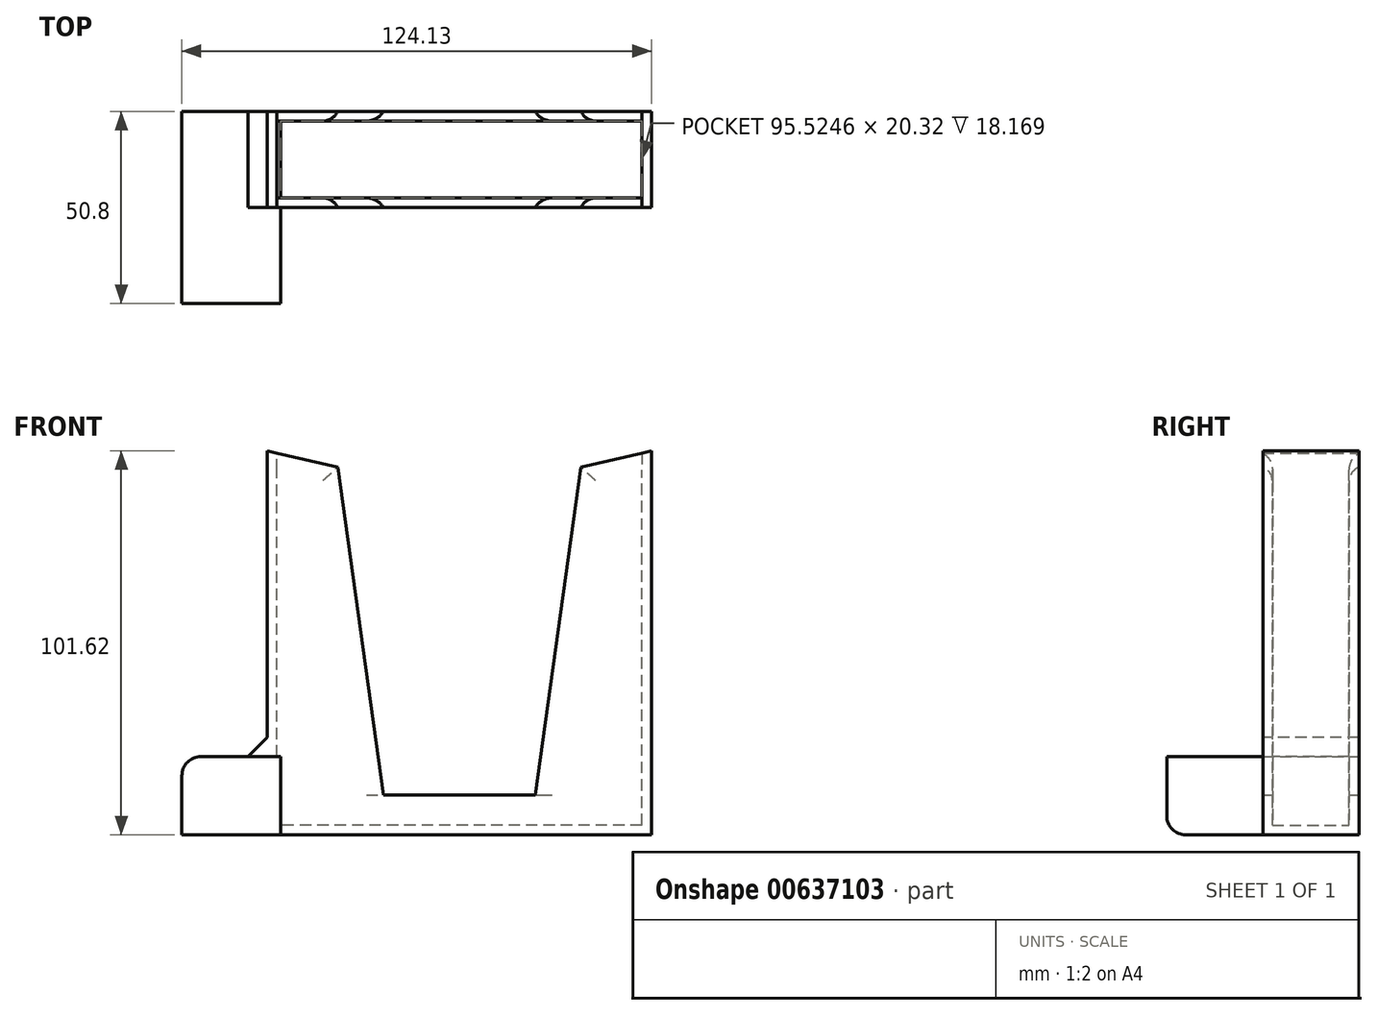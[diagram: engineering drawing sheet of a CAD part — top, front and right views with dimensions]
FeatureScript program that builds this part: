
annotation { "Feature Type Name" : "Feature", "Feature Type Description" : "" }
export const myFeature = defineFeature(function(context is Context, id is Id, definition is map)
    precondition{}
    {
        {
            var Q0;
            Q0=qCreatedBy(makeId("Front.planeOp"),FACE);
            var sketch = newSketch(context, id + "F0", { "sketchPlane" : qUnion([Q0])});
            skLineSegment(sketch, "E0.bottom", {"start": v(50.8, -50.8) * mm, "end": v(-50.8, -50.8) * mm});
            skLineSegment(sketch, "E0.top", {"start": v(50.8, 50.8) * mm, "end": v(-50.8, 50.8) * mm});
            skLineSegment(sketch, "E0.left", {"start": v(50.8, -50.8) * mm, "end": v(50.8, 50.8) * mm});
            skLineSegment(sketch, "E0.right", {"start": v(-50.8, -50.8) * mm, "end": v(-50.8, 50.8) * mm});
            skPoint(sketch, "E0.middle", {"position": v(0, 0) * mm});
            skLineSegment(sketch, "E1.bottom", {"start": v(-20.08, -40.32) * mm, "end": v(20.08, -40.32) * mm});
            skLineSegment(sketch, "E1.top", {"start": v(-20.08, 40.32) * mm, "end": v(20.08, 40.32) * mm});
            skLineSegment(sketch, "E1.left", {"start": v(-20.08, -40.32) * mm, "end": v(-20.08, 40.32) * mm});
            skLineSegment(sketch, "E1.right", {"start": v(20.08, -40.32) * mm, "end": v(20.08, 40.32) * mm});
            skLineSegment(sketch, "E2.bottom", {"start": v(-32.13, 46.49) * mm, "end": v(32.13, 46.49) * mm});
            skLineSegment(sketch, "E2.top", {"start": v(-32.13, 55.11) * mm, "end": v(32.13, 55.11) * mm});
            skLineSegment(sketch, "E2.left", {"start": v(-32.13, 46.49) * mm, "end": v(-32.13, 55.11) * mm});
            skLineSegment(sketch, "E2.right", {"start": v(32.13, 46.49) * mm, "end": v(32.13, 55.11) * mm});
            skPoint(sketch, "E2.middle", {"position": v(0, 50.8) * mm});
            skLineSegment(sketch, "E3", {"start": v(-50.8, 50.8) * mm, "end": v(-32.13, 46.49) * mm});
            skLineSegment(sketch, "E4", {"start": v(-20.08, 40.32) * mm, "end": v(-20.08, 30.12) * mm});
            skLineSegment(sketch, "E5", {"start": v(-32.13, 46.49) * mm, "end": v(-20.08, -40.32) * mm});
            skLineSegment(sketch, "E6", {"start": v(20.08, -40.32) * mm, "end": v(32.13, 46.49) * mm});
            skLineSegment(sketch, "E7", {"start": v(50.8, 50.8) * mm, "end": v(32.13, 46.49) * mm});
            skSolve(sketch);
        }
        {
            var Q0;
            Q0=makeQuery(id+"F0.imprint","IMPRINT",FACE,{"disambiguationData":[TD([[makeQuery(id+"F0.imprint","IMPRINT",EDGE,{"derivedFrom":sQuery(id+"F0.wireOp",EDGE,"E0.bottom")}),-1.0]])]});
            extrude(context, id + "F1", {"entities" : qUnion([Q0]), "depth" : 25.4 * mm, "offsetDistance" : 25.4 * mm});
        }
        {
            var Q0;
            Q0=makeQuery(id+"F1.opExtrude","SWEPT_FACE",FACE,{"disambiguationData":[OSD([sQuery(id+"F0.wireOp",EDGE,"E3")])]});
            var Q1;
            Q1=makeQuery(id+"F1.opExtrude","SWEPT_FACE",FACE,{"disambiguationData":[OSD([sQuery(id+"F0.wireOp",EDGE,"E5")])]});
            var Q2;
            Q2=makeQuery(id+"F1.opExtrude","SWEPT_FACE",FACE,{"disambiguationData":[OSD([sQuery(id+"F0.wireOp",EDGE,"E1.bottom")])]});
            var Q3;
            Q3=makeQuery(id+"F1.opExtrude","SWEPT_FACE",FACE,{"disambiguationData":[OSD([sQuery(id+"F0.wireOp",EDGE,"E7")])]});
            var Q4;
            Q4=makeQuery(id+"F1.opExtrude","SWEPT_FACE",FACE,{"disambiguationData":[OSD([sQuery(id+"F0.wireOp",EDGE,"E6")])]});
            shell(context, id + "F2", {"entities" : qUnion([Q0, Q1, Q2, Q3, Q4]), "thickness" : 2.54 * mm});
        }
        {
            var Q0;
            {var subQ0=sQuery(id+"F0.wireOp",EDGE,"E6");Q0=makeQuery(id+"F2.opShell","OFFSET_EDGE",EDGE,{"disambiguationData":[OSD([subQ0]),TDD([makeQuery(id+"F1.opExtrude","CAP_EDGE",EDGE,{"disambiguationData":[OSD([subQ0])],"isStart":true})])]});}
            var Q1;
            {var subQ0=sQuery(id+"F0.wireOp",EDGE,"E5");Q1=makeQuery(id+"F2.opShell","OFFSET_EDGE",EDGE,{"disambiguationData":[OSD([subQ0]),TDD([makeQuery(id+"F1.opExtrude","CAP_EDGE",EDGE,{"disambiguationData":[OSD([subQ0])],"isStart":true})])]});}
            var Q2;
            {var subQ0=sQuery(id+"F0.wireOp",EDGE,"E7");Q2=makeQuery(id+"F2.opShell","OFFSET_EDGE",EDGE,{"disambiguationData":[OSD([subQ0]),TDD([makeQuery(id+"F1.opExtrude","CAP_EDGE",EDGE,{"disambiguationData":[OSD([subQ0])],"isStart":true})])]});}
            var Q3;
            {var subQ0=sQuery(id+"F0.wireOp",EDGE,"E3");Q3=makeQuery(id+"F2.opShell","OFFSET_EDGE",EDGE,{"disambiguationData":[OSD([subQ0]),TDD([makeQuery(id+"F1.opExtrude","CAP_EDGE",EDGE,{"disambiguationData":[OSD([subQ0])],"isStart":true})])]});}
            var Q4;
            {var subQ0=sQuery(id+"F0.wireOp",EDGE,"E5");Q4=makeQuery(id+"F2.opShell","OFFSET_EDGE",EDGE,{"disambiguationData":[OSD([subQ0]),TDD([makeQuery(id+"F1.opExtrude","CAP_EDGE",EDGE,{"disambiguationData":[OSD([subQ0])],"isStart":false})])]});}
            var Q5;
            {var subQ0=sQuery(id+"F0.wireOp",EDGE,"E3");Q5=makeQuery(id+"F2.opShell","OFFSET_EDGE",EDGE,{"disambiguationData":[OSD([subQ0]),TDD([makeQuery(id+"F1.opExtrude","CAP_EDGE",EDGE,{"disambiguationData":[OSD([subQ0])],"isStart":false})])]});}
            var Q6;
            {var subQ0=sQuery(id+"F0.wireOp",EDGE,"E6");Q6=makeQuery(id+"F2.opShell","OFFSET_EDGE",EDGE,{"disambiguationData":[OSD([subQ0]),TDD([makeQuery(id+"F1.opExtrude","CAP_EDGE",EDGE,{"disambiguationData":[OSD([subQ0])],"isStart":false})])]});}
            var Q7;
            {var subQ0=sQuery(id+"F0.wireOp",EDGE,"E7");Q7=makeQuery(id+"F2.opShell","OFFSET_EDGE",EDGE,{"disambiguationData":[OSD([subQ0]),TDD([makeQuery(id+"F1.opExtrude","CAP_EDGE",EDGE,{"disambiguationData":[OSD([subQ0])],"isStart":false})])]});}
            fillet(context, id + "F3", {"entities" : qUnion([Q0, Q1, Q2, Q3, Q4, Q5, Q6, Q7]), "radius" : 5.08 * mm, "tangentPropagation" : true, "allowEdgeOverflow" : false});
        }
        {
            var Q0;
            Q0=qCreatedBy(makeId("Front.planeOp"),FACE);
            var sketch = newSketch(context, id + "F4", { "sketchPlane" : qUnion([Q0])});
            skLineSegment(sketch, "E8.bottom", {"start": v(-47.26, -50.82) * mm, "end": v(-54.84, -50.82) * mm});
            skLineSegment(sketch, "E8.top", {"start": v(-47.26, -43.25) * mm, "end": v(-54.84, -43.25) * mm});
            skLineSegment(sketch, "E8.left", {"start": v(-47.26, -50.82) * mm, "end": v(-47.26, -43.25) * mm});
            skLineSegment(sketch, "E8.right", {"start": v(-54.84, -50.82) * mm, "end": v(-54.84, -43.25) * mm});
            skLineSegment(sketch, "E9.bottom", {"start": v(-47.26, -50.82) * mm, "end": v(-73.33, -50.82) * mm});
            skLineSegment(sketch, "E9.top", {"start": v(-47.26, -30.1) * mm, "end": v(-73.33, -30.1) * mm});
            skLineSegment(sketch, "E9.left", {"start": v(-47.26, -50.82) * mm, "end": v(-47.26, -30.1) * mm});
            skLineSegment(sketch, "E9.right", {"start": v(-73.33, -50.82) * mm, "end": v(-73.33, -30.1) * mm});
            skSolve(sketch);
        }
        {
            var Q0;
            {var subQ4=sQuery(id+"F4.wireOp",EDGE,"E8.top");Q0=makeQuery(id+"F4.imprint","IMPRINT",FACE,{"disambiguationData":[TD([[makeQuery(id+"F4.imprint","IMPRINT",EDGE,{"derivedFrom":subQ4}),-1.0]])]});}
            var Q1;
            {var subQ0=sQuery(id+"F4.wireOp",EDGE,"E8.top");Q1=makeQuery(id+"F4.imprint","IMPRINT",FACE,{"disambiguationData":[TD([[makeQuery(id+"F4.imprint","IMPRINT",EDGE,{"derivedFrom":subQ0}),1.0]])]});}
            extrude(context, id + "F5", {"entities" : qUnion([Q0, Q1]), "operationType" : NewBodyOperationType.ADD, "depth" : 50.8 * mm, "offsetDistance" : 25.4 * mm});
        }
        {
            var Q0;
            Q0=makeQuery(id+"F5.boolean.opBoolean","INTERSECT",EDGE,{"derivedFrom":[makeQuery(id+"F1.opExtrude","SWEPT_FACE",FACE,{"disambiguationData":[OSD([sQuery(id+"F0.wireOp",EDGE,"E0.right")])]}),makeQuery(id+"F5.opExtrude","SWEPT_FACE",FACE,{"disambiguationData":[OSD([sQuery(id+"F4.wireOp",EDGE,"E9.top")])]})]});
            chamfer(context, id + "F6", {"entities" : qUnion([Q0]), "width" : 5.08 * mm, "tangentPropagation" : true});
        }
        {
            var Q0;
            Q0=makeQuery(id+"F5.opExtrude","SWEPT_EDGE",EDGE,{"disambiguationData":[OSD([sQuery(id+"F4.wireOp",EDGE,"E9.top"),sQuery(id+"F4.wireOp",EDGE,"E9.right")])]});
            var Q1;
            Q1=makeQuery(id+"F5.opExtrude","CAP_EDGE",EDGE,{"disambiguationData":[OSD([sQuery(id+"F4.wireOp",EDGE,"E9.bottom")])],"isStart":false});
            fillet(context, id + "F7", {"entities" : qUnion([Q0, Q1]), "radius" : 5.08 * mm, "tangentPropagation" : true, "allowEdgeOverflow" : false});
        }
    });
